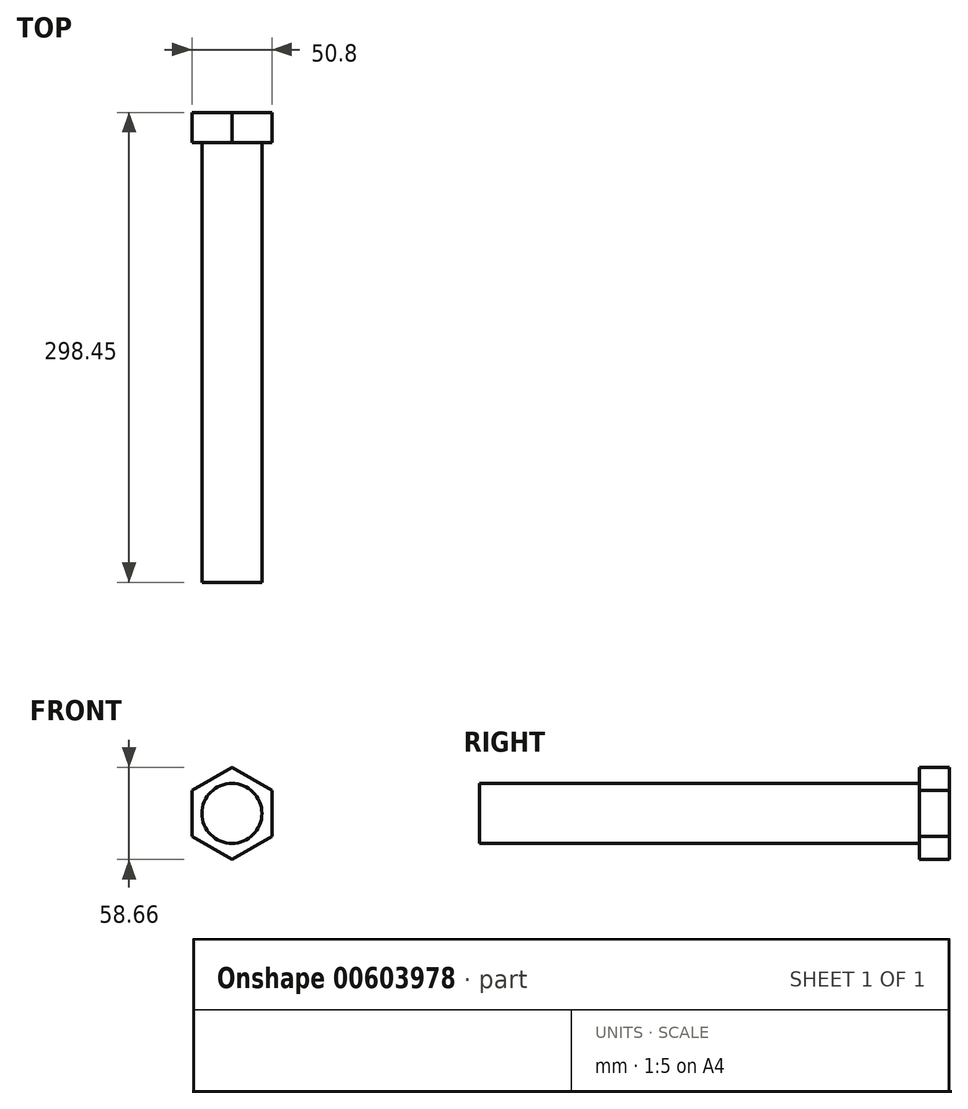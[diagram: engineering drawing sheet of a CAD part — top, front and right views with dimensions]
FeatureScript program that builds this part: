
annotation { "Feature Type Name" : "Feature", "Feature Type Description" : "" }
export const myFeature = defineFeature(function(context is Context, id is Id, definition is map)
    precondition{}
    {
        {
            var Q0;
            Q0=qCreatedBy(makeId("Front.planeOp"),FACE);
            var sketch = newSketch(context, id + "F0", { "sketchPlane" : qUnion([Q0])});
            skCircle(sketch, "E0", {"center": v(0, 0) * mm, "radius": 19.05 * mm});
            skSolve(sketch);
        }
        {
            var Q0;
            Q0 = qSketchRegion(id + "F0", true);
            extrude(context, id + "F1", {"entities" : qUnion([Q0]), "depth" : 279.4 * mm, "offsetDistance" : 25.4 * mm});
        }
        {
            var Q0;
            Q0=makeQuery(id+"F1.opExtrude","CAP_FACE",FACE,{"disambiguationData":[OSD([sQuery(id+"F0.wireOp",EDGE,"E0")])],"isStart":true});
            var sketch = newSketch(context, id + "F2", { "sketchPlane" : qUnion([Q0])});
            skCircle(sketch, "E1.cCircle", {"center": v(0, 0) * mm, "radius": 25.4 * mm, "construction": true});
            skLineSegment(sketch, "E1.0", {"start": v(25.4, 14.66) * mm, "end": v(25.4, -14.66) * mm});
            skLineSegment(sketch, "E1.1", {"start": v(25.4, -14.66) * mm, "end": v(0, -29.33) * mm});
            skLineSegment(sketch, "E1.2", {"start": v(0, -29.33) * mm, "end": v(-25.4, -14.66) * mm});
            skLineSegment(sketch, "E1.3", {"start": v(-25.4, -14.66) * mm, "end": v(-25.4, 14.66) * mm});
            skLineSegment(sketch, "E1.4", {"start": v(-25.4, 14.66) * mm, "end": v(0, 29.33) * mm});
            skLineSegment(sketch, "E1.5", {"start": v(0, 29.33) * mm, "end": v(25.4, 14.66) * mm});
            skPoint(sketch, "E1.0.midPoint", {"position": v(25.4, 0) * mm});
            skSolve(sketch);
        }
        {
            var Q0;
            Q0 = qSketchRegion(id + "F2", true);
            extrude(context, id + "F3", {"entities" : qUnion([Q0]), "operationType" : NewBodyOperationType.ADD, "depth" : 19.05 * mm, "offsetDistance" : 25.4 * mm});
        }
    });
